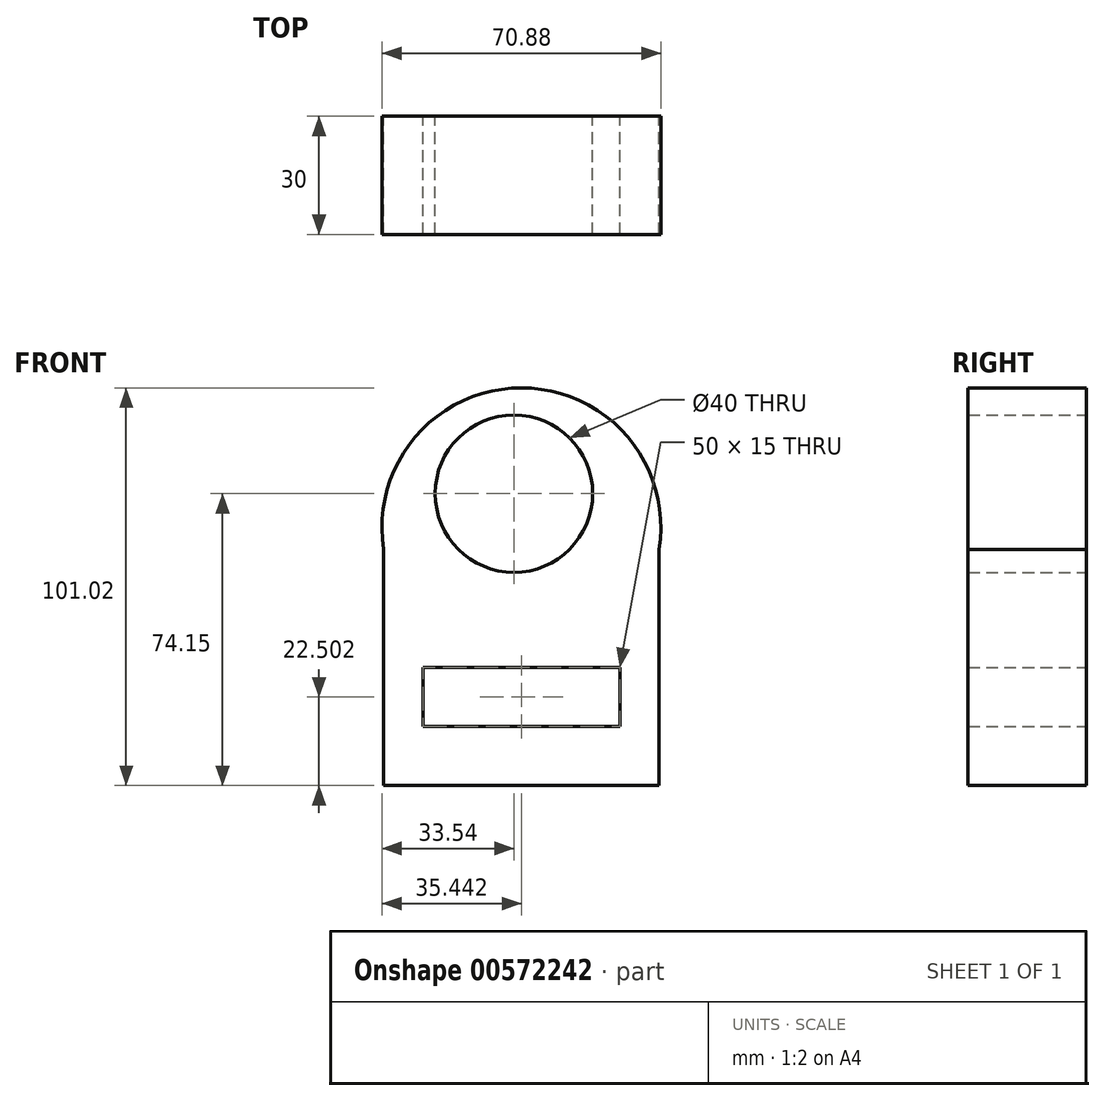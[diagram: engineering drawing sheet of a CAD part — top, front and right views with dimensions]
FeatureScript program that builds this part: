
annotation { "Feature Type Name" : "Feature", "Feature Type Description" : "" }
export const myFeature = defineFeature(function(context is Context, id is Id, definition is map)
    precondition{}
    {
        {
            var Q0;
            Q0=qCreatedBy(makeId("Front.planeOp"),FACE);
            var sketch = newSketch(context, id + "F0", { "sketchPlane" : qUnion([Q0])});
            skCircle(sketch, "E0", {"center": v(0, 20.04) * mm, "radius": 20 * mm});
            skLineSegment(sketch, "E1", {"start": v(-33.1, -54.1) * mm, "end": v(36.9, -54.1) * mm});
            skLineSegment(sketch, "E2", {"start": v(36.9, -54.1) * mm, "end": v(36.9, 5.9) * mm});
            skLineSegment(sketch, "E3", {"start": v(-33.1, -54.1) * mm, "end": v(-33.1, 5.9) * mm});
            skArc(sketch, "E4", {"start": v(36.9, 5.9) * mm, "mid": v(1.9, 46.91) * mm, "end": v(-33.1, 5.9) * mm});
            skLineSegment(sketch, "E5.bottom", {"start": v(-23.1, -24.1) * mm, "end": v(26.9, -24.1) * mm});
            skLineSegment(sketch, "E5.top", {"start": v(-23.1, -39.1) * mm, "end": v(26.9, -39.1) * mm});
            skLineSegment(sketch, "E5.left", {"start": v(-23.1, -24.1) * mm, "end": v(-23.1, -39.1) * mm});
            skLineSegment(sketch, "E5.right", {"start": v(26.9, -24.1) * mm, "end": v(26.9, -39.1) * mm});
            skSolve(sketch);
        }
        {
            var Q0;
            Q0 = qSketchRegion(id + "F0", true);
            extrude(context, id + "F1", {"entities" : qUnion([Q0]), "depth" : 30 * mm, "offsetDistance" : 25 * mm});
        }
    });
